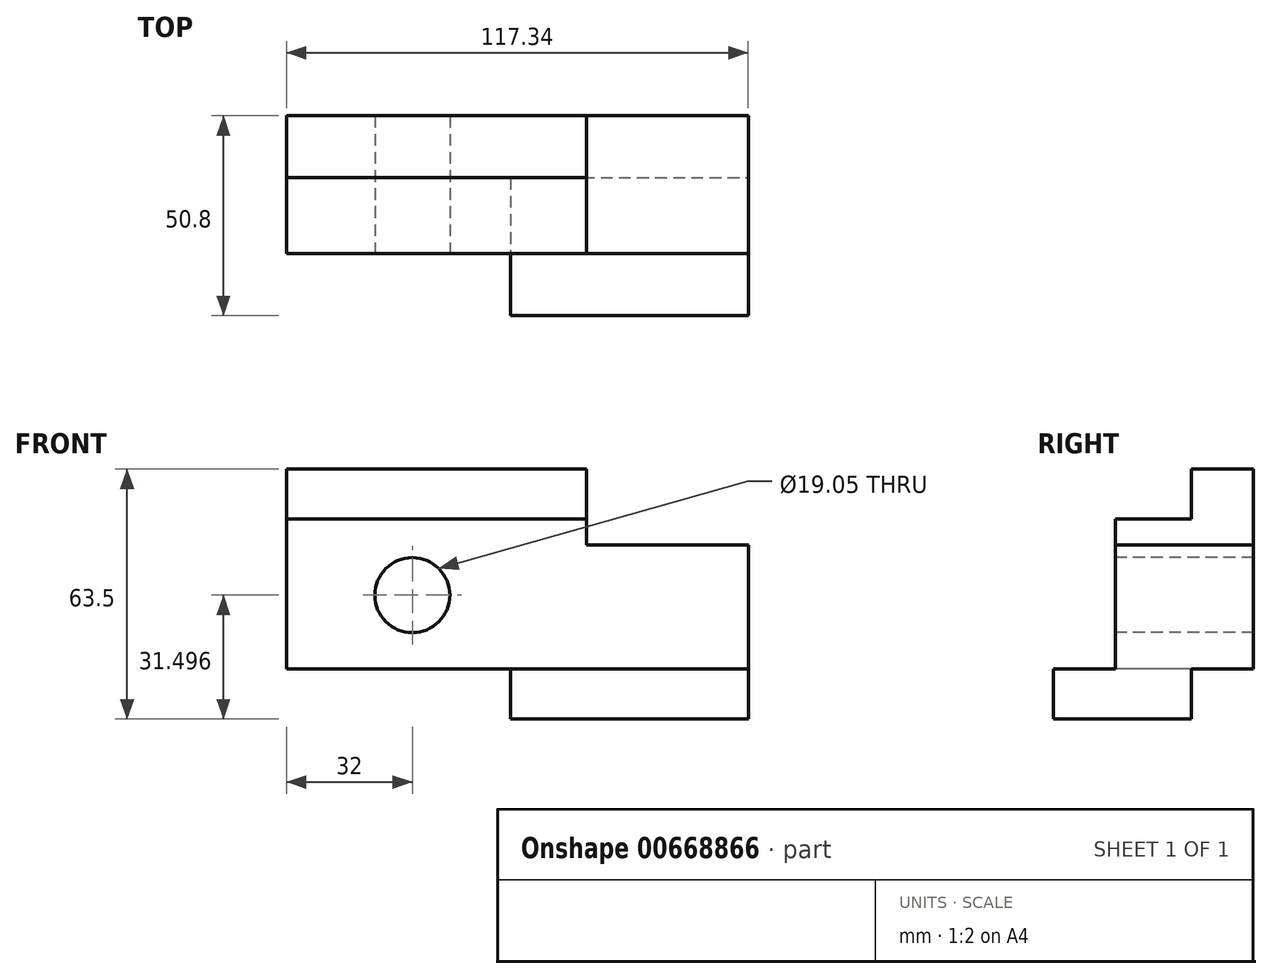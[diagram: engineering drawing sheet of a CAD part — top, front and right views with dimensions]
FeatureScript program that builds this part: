
annotation { "Feature Type Name" : "Feature", "Feature Type Description" : "" }
export const myFeature = defineFeature(function(context is Context, id is Id, definition is map)
    precondition{}
    {
        {
            var Q0;
            Q0=qCreatedBy(makeId("Front.planeOp"),FACE);
            var sketch = newSketch(context, id + "F0", { "sketchPlane" : qUnion([Q0])});
            skLineSegment(sketch, "E0.bottom", {"start": v(-58.67, 31.75) * mm, "end": v(58.67, 31.75) * mm});
            skLineSegment(sketch, "E0.top", {"start": v(-58.67, -31.75) * mm, "end": v(58.67, -31.75) * mm});
            skLineSegment(sketch, "E0.left", {"start": v(-58.67, 31.75) * mm, "end": v(-58.67, -31.75) * mm});
            skLineSegment(sketch, "E0.right", {"start": v(58.67, 31.75) * mm, "end": v(58.67, -31.75) * mm});
            skPoint(sketch, "E0.middle", {"position": v(0, 0) * mm});
            skSolve(sketch);
        }
        {
            var Q0;
            Q0 = qSketchRegion(id + "F0", true);
            extrude(context, id + "F1", {"entities" : qUnion([Q0]), "depth" : 50.8 * mm, "offsetDistance" : 25.4 * mm});
        }
        {
            var Q0;
            Q0=makeQuery(id+"F1.opExtrude","CAP_FACE",FACE,{"disambiguationData":[OSD([sQuery(id+"F0.wireOp",EDGE,"E0.bottom"),sQuery(id+"F0.wireOp",EDGE,"E0.top"),sQuery(id+"F0.wireOp",EDGE,"E0.left"),sQuery(id+"F0.wireOp",EDGE,"E0.right")])],"isStart":false});
            var sketch = newSketch(context, id + "F2", { "sketchPlane" : qUnion([Q0])});
            skLineSegment(sketch, "E1.bottom", {"start": v(-58.67, -31.75) * mm, "end": v(-1.78, -31.75) * mm});
            skLineSegment(sketch, "E1.top", {"start": v(-58.67, -19.05) * mm, "end": v(-1.78, -19.05) * mm});
            skLineSegment(sketch, "E1.left", {"start": v(-58.67, -31.75) * mm, "end": v(-58.67, -19.05) * mm});
            skLineSegment(sketch, "E1.right", {"start": v(-1.78, -31.75) * mm, "end": v(-1.78, -19.05) * mm});
            skSolve(sketch);
        }
        {
            var Q0;
            Q0 = qSketchRegion(id + "F2", true);
            extrude(context, id + "F3", {"entities" : qUnion([Q0]), "operationType" : NewBodyOperationType.REMOVE, "oppositeDirection" : true, "depth" : 50.8 * mm, "offsetDistance" : 25.4 * mm});
        }
        {
            var Q0;
            Q0=makeQuery(id+"F1.opExtrude","CAP_FACE",FACE,{"disambiguationData":[OSD([sQuery(id+"F0.wireOp",EDGE,"E0.bottom"),sQuery(id+"F0.wireOp",EDGE,"E0.top"),sQuery(id+"F0.wireOp",EDGE,"E0.left"),sQuery(id+"F0.wireOp",EDGE,"E0.right")])],"isStart":false});
            var sketch = newSketch(context, id + "F4", { "sketchPlane" : qUnion([Q0])});
            skLineSegment(sketch, "E2.bottom", {"start": v(-58.67, 31.75) * mm, "end": v(58.67, 31.75) * mm});
            skLineSegment(sketch, "E2.top", {"start": v(-58.67, -19.05) * mm, "end": v(58.67, -19.05) * mm});
            skLineSegment(sketch, "E2.left", {"start": v(-58.67, 31.75) * mm, "end": v(-58.67, -19.05) * mm});
            skLineSegment(sketch, "E2.right", {"start": v(58.67, 31.75) * mm, "end": v(58.67, -19.05) * mm});
            skSolve(sketch);
        }
        {
            var Q0;
            Q0=makeQuery(id+"F4.imprint","IMPRINT",FACE,{"disambiguationData":[TD([[makeQuery(id+"F4.imprint","IMPRINT",EDGE,{"derivedFrom":sQuery(id+"F4.wireOp",EDGE,"E2.bottom")}),-1.0]])]});
            extrude(context, id + "F5", {"entities" : qUnion([Q0]), "operationType" : NewBodyOperationType.REMOVE, "oppositeDirection" : true, "depth" : 15.75 * mm, "offsetDistance" : 25.4 * mm});
        }
        {
            var Q0;
            Q0=makeQuery(id+"F5.boolean.opBoolean","COPY",FACE,{"derivedFrom":makeQuery(id+"F5.opExtrude","CAP_FACE",FACE,{"disambiguationData":[OSD([sQuery(id+"F4.wireOp",EDGE,"E2.bottom"),sQuery(id+"F4.wireOp",EDGE,"E2.top"),sQuery(id+"F4.wireOp",EDGE,"E2.left"),sQuery(id+"F4.wireOp",EDGE,"E2.right")])],"isStart":false})});
            var sketch = newSketch(context, id + "F6", { "sketchPlane" : qUnion([Q0])});
            skCircle(sketch, "E3", {"center": v(-26.67, -0.25) * mm, "radius": 9.53 * mm});
            skPoint(sketch, "E3.first.point", {"position": v(-30.49, 8.47) * mm});
            skPoint(sketch, "E3.second.point", {"position": v(-17.15, 0) * mm});
            skPoint(sketch, "E3.third.point", {"position": v(-17.73, 3.05) * mm});
            skSolve(sketch);
        }
        {
            var Q0;
            Q0 = qSketchRegion(id + "F6", true);
            extrude(context, id + "F7", {"entities" : qUnion([Q0]), "operationType" : NewBodyOperationType.REMOVE, "endBound" : BoundingType.THROUGH_ALL, "oppositeDirection" : true, "depth" : 25.4 * mm, "offsetDistance" : 25.4 * mm});
        }
        {
            var Q0;
            Q0=makeQuery(id+"F1.opExtrude","SWEPT_FACE",FACE,{"disambiguationData":[OSD([sQuery(id+"F0.wireOp",EDGE,"E0.right")])]});
            var sketch = newSketch(context, id + "F8", { "sketchPlane" : qUnion([Q0])});
            skLineSegment(sketch, "E4.bottom", {"start": v(0, -31.75) * mm, "end": v(-15.75, -31.75) * mm});
            skLineSegment(sketch, "E4.top", {"start": v(0, -19.05) * mm, "end": v(-15.75, -19.05) * mm});
            skLineSegment(sketch, "E4.left", {"start": v(0, -31.75) * mm, "end": v(0, -19.05) * mm});
            skLineSegment(sketch, "E4.right", {"start": v(-15.75, -31.75) * mm, "end": v(-15.75, -19.05) * mm});
            skSolve(sketch);
        }
        {
            var Q0;
            Q0=makeQuery(id+"F8.imprint","IMPRINT",FACE,{"disambiguationData":[TD([[makeQuery(id+"F8.imprint","IMPRINT",EDGE,{"derivedFrom":sQuery(id+"F8.wireOp",EDGE,"E4.bottom")}),1.0]])]});
            extrude(context, id + "F9", {"entities" : qUnion([Q0]), "operationType" : NewBodyOperationType.REMOVE, "endBound" : BoundingType.THROUGH_ALL, "oppositeDirection" : true, "depth" : 25.4 * mm, "offsetDistance" : 25.4 * mm});
        }
        {
            var Q0;
            Q0=makeQuery(id+"F1.opExtrude","SWEPT_FACE",FACE,{"disambiguationData":[OSD([sQuery(id+"F0.wireOp",EDGE,"E0.bottom")])]});
            var sketch = newSketch(context, id + "F10", { "sketchPlane" : qUnion([Q0])});
            skLineSegment(sketch, "E5.bottom", {"start": v(58.67, -35.05) * mm, "end": v(17.53, -35.05) * mm});
            skLineSegment(sketch, "E5.top", {"start": v(58.67, 0) * mm, "end": v(17.53, 0) * mm});
            skLineSegment(sketch, "E5.left", {"start": v(58.67, -35.05) * mm, "end": v(58.67, 0) * mm});
            skLineSegment(sketch, "E5.right", {"start": v(17.53, -35.05) * mm, "end": v(17.53, 0) * mm});
            skSolve(sketch);
        }
        {
            var Q0;
            Q0=makeQuery(id+"F10.imprint","IMPRINT",FACE,{"disambiguationData":[TD([[makeQuery(id+"F10.imprint","IMPRINT",EDGE,{"derivedFrom":sQuery(id+"F10.wireOp",EDGE,"E5.bottom")}),1.0]])]});
            extrude(context, id + "F11", {"entities" : qUnion([Q0]), "operationType" : NewBodyOperationType.REMOVE, "oppositeDirection" : true, "depth" : 19.3 * mm, "offsetDistance" : 25.4 * mm});
        }
        {
            var Q0;
            Q0=makeQuery(id+"F11.boolean.opBoolean","COPY",FACE,{"derivedFrom":makeQuery(id+"F11.opExtrude","SWEPT_FACE",FACE,{"disambiguationData":[OSD([sQuery(id+"F10.wireOp",EDGE,"E5.right")])]})});
            var sketch = newSketch(context, id + "F12", { "sketchPlane" : qUnion([Q0])});
            skLineSegment(sketch, "E6.bottom", {"start": v(-35.05, 31.75) * mm, "end": v(-15.75, 31.75) * mm});
            skLineSegment(sketch, "E6.top", {"start": v(-35.05, 19.05) * mm, "end": v(-15.75, 19.05) * mm});
            skLineSegment(sketch, "E6.left", {"start": v(-35.05, 31.75) * mm, "end": v(-35.05, 19.05) * mm});
            skLineSegment(sketch, "E6.right", {"start": v(-15.75, 31.75) * mm, "end": v(-15.75, 19.05) * mm});
            skSolve(sketch);
        }
        {
            var Q0;
            Q0 = qSketchRegion(id + "F12", true);
            extrude(context, id + "F13", {"entities" : qUnion([Q0]), "operationType" : NewBodyOperationType.REMOVE, "endBound" : BoundingType.THROUGH_ALL, "oppositeDirection" : true, "depth" : 25.4 * mm, "offsetDistance" : 25.4 * mm});
        }
    });
